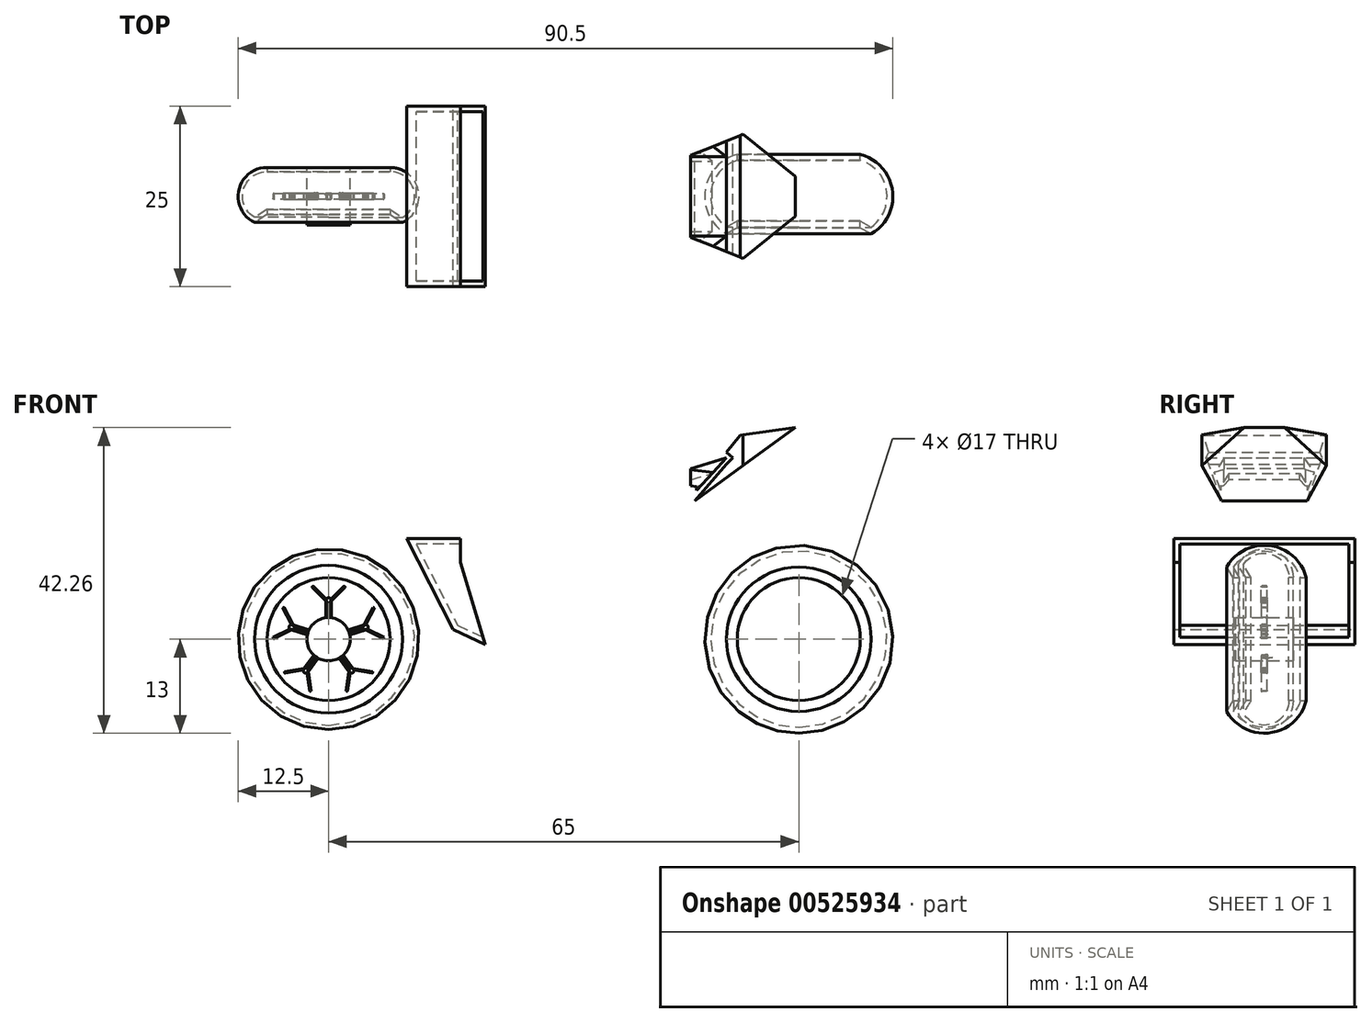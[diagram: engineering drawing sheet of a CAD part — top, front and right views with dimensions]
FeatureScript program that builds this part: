
annotation { "Feature Type Name" : "Feature", "Feature Type Description" : "" }
export const myFeature = defineFeature(function(context is Context, id is Id, definition is map)
    precondition{}
    {
        {
            var Q0;
            Q0=qCreatedBy(makeId("Front.planeOp"),FACE);
            var sketch = newSketch(context, id + "F0", { "sketchPlane" : qUnion([Q0])});
            skLineSegment(sketch, "E0", {"start": v(-48.54, 40.92) * mm, "end": v(-35.82, 48.8) * mm});
            skLineSegment(sketch, "E1", {"start": v(-21.42, 44.3) * mm, "end": v(-22.33, 41.37) * mm});
            skLineSegment(sketch, "E2", {"start": v(-12, 31.76) * mm, "end": v(-48.54, 40.92) * mm});
            skLineSegment(sketch, "E3", {"start": v(-35.82, 48.8) * mm, "end": v(-31.87, 48.8) * mm});
            skLineSegment(sketch, "E4", {"start": v(-31.87, 48.8) * mm, "end": v(-21.42, 44.3) * mm});
            skLineSegment(sketch, "E5", {"start": v(-22.33, 39.52) * mm, "end": v(-12, 31.76) * mm});
            skLineSegment(sketch, "E6", {"start": v(-22.33, 41.37) * mm, "end": v(-22.8, 39.87) * mm});
            skLineSegment(sketch, "E7", {"start": v(-22.33, 39.52) * mm, "end": v(-22.8, 39.87) * mm});
            skPoint(sketch, "E8.orphan", {"position": v(-22.9, 39.52) * mm});
            skPoint(sketch, "E9.orphan", {"position": v(-22.9, 39.95) * mm});
            skSolve(sketch);
        }
        {
            var Q0;
            Q0 = qSketchRegion(id + "F0", true);
            var Q1;
            Q1=makeQuery(id+"F0.imprint","IMPRINT",FACE,{"disambiguationData":[TD([[makeQuery(id+"F0.imprint","IMPRINT",EDGE,{"derivedFrom":sQuery(id+"F0.wireOp",EDGE,"E0")}),-1.0]])]});
            extrude(context, id + "F1", {"entities" : qUnion([Q0, Q1]), "endBound" : BoundingType.SYMMETRIC, "depth" : 16 * mm, "offsetDistance" : 25 * mm});
        }
        {
            var Q0;
            Q0=qCreatedBy(makeId("Front.planeOp"),FACE);
            var sketch = newSketch(context, id + "F2", { "sketchPlane" : qUnion([Q0])});
            skLineSegment(sketch, "E10", {"start": v(-46.44, 40.35) * mm, "end": v(-50.24, 36.38) * mm});
            skLineSegment(sketch, "E11", {"start": v(-50.24, 36.38) * mm, "end": v(-45.14, 33.46) * mm});
            skLineSegment(sketch, "E12", {"start": v(-45.14, 33.46) * mm, "end": v(-37.05, 33.46) * mm});
            skLineSegment(sketch, "E13", {"start": v(-37.05, 33.46) * mm, "end": v(-32.75, 37.72) * mm});
            skLineSegment(sketch, "E14", {"start": v(-32.75, 37.72) * mm, "end": v(-41.1, 39.88) * mm});
            skPoint(sketch, "E14.endSnap0", {"position": v(-41.1, 33.46) * mm});
            skLineSegment(sketch, "E15", {"start": v(-46.44, 40.35) * mm, "end": v(-41.51, 41.54) * mm});
            skLineSegment(sketch, "E16", {"start": v(-41.51, 41.54) * mm, "end": v(-37.94, 45.76) * mm});
            skArc(sketch, "E17", {"start": v(-23.53, 44.5) * mm, "mid": v(-30.85, 43.12) * mm, "end": v(-36.92, 38.8) * mm});
            skFitSpline(sketch, "E18", {"points": [v(-37.94, 45.76) * mm, v(-36.16, 46.98) * mm, v(-33.88, 47.49) * mm, v(-31.31, 47.24) * mm, v(-23.53, 44.5) * mm], "startDerivative": vector(8.49, 6.98) * mm, "endDerivative": vector(23.02, -8.95) * mm});
            skSolve(sketch);
        }
        {
            var Q0;
            Q0=makeQuery(id+"F2.imprint","IMPRINT",FACE,{"disambiguationData":[TD([[makeQuery(id+"F2.imprint","IMPRINT",EDGE,{"derivedFrom":sQuery(id+"F2.wireOp",EDGE,"E10")}),1.0]])]});
            extrude(context, id + "F3", {"entities" : qUnion([Q0]), "operationType" : NewBodyOperationType.ADD, "endBound" : BoundingType.SYMMETRIC, "depth" : 25 * mm, "offsetDistance" : 25 * mm});
        }
        {
            var Q0;
            Q0=makeQuery(id+"F1.opExtrude","SWEPT_EDGE",EDGE,{"disambiguationData":[OSD([sQuery(id+"F0.wireOp",EDGE,"E1"),sQuery(id+"F0.wireOp",EDGE,"E4")])]});
            fillet(context, id + "F4", {"entities" : qUnion([Q0]), "radius" : 2 * mm, "tangentPropagation" : true, "allowEdgeOverflow" : false});
        }
        {
            var Q0;
            Q0=makeQuery(id+"F1.opExtrude","SWEPT_EDGE",EDGE,{"disambiguationData":[OSD([sQuery(id+"F0.wireOp",EDGE,"E6"),sQuery(id+"F0.wireOp",EDGE,"E7")])]});
            fillet(context, id + "F5", {"entities" : qUnion([Q0]), "radius" : 2 * mm, "tangentPropagation" : true, "allowEdgeOverflow" : false});
        }
        {
            var Q0;
            Q0=makeQuery(id+"F3.opExtrude","CAP_EDGE",EDGE,{"disambiguationData":[OSD([sQuery(id+"F2.wireOp",EDGE,"E13")])],"isStart":false});
            var Q1;
            Q1=makeQuery(id+"F3.opExtrude","CAP_EDGE",EDGE,{"disambiguationData":[OSD([sQuery(id+"F2.wireOp",EDGE,"E12")])],"isStart":false});
            var Q2;
            Q2=makeQuery(id+"F3.opExtrude","CAP_EDGE",EDGE,{"disambiguationData":[OSD([sQuery(id+"F2.wireOp",EDGE,"E10")])],"isStart":false});
            var Q3;
            Q3=makeQuery(id+"F3.opExtrude","CAP_EDGE",EDGE,{"disambiguationData":[OSD([sQuery(id+"F2.wireOp",EDGE,"E11")])],"isStart":false});
            var Q4;
            Q4=makeQuery(id+"F3.opExtrude","CAP_EDGE",EDGE,{"disambiguationData":[OSD([sQuery(id+"F2.wireOp",EDGE,"E13")])],"isStart":true});
            var Q5;
            Q5=makeQuery(id+"F3.opExtrude","CAP_EDGE",EDGE,{"disambiguationData":[OSD([sQuery(id+"F2.wireOp",EDGE,"E12")])],"isStart":true});
            var Q6;
            Q6=makeQuery(id+"F3.opExtrude","CAP_EDGE",EDGE,{"disambiguationData":[OSD([sQuery(id+"F2.wireOp",EDGE,"E11")])],"isStart":true});
            var Q7;
            Q7=makeQuery(id+"F3.opExtrude","CAP_EDGE",EDGE,{"disambiguationData":[OSD([sQuery(id+"F2.wireOp",EDGE,"E10")])],"isStart":true});
            chamfer(context, id + "F6", {"entities" : qUnion([Q0, Q1, Q2, Q3, Q4, Q5, Q6, Q7]), "width" : 3 * mm, "tangentPropagation" : true});
        }
        {
            var Q0;
            Q0=qCreatedBy(makeId("Top.planeOp"),FACE);
            var sketch = newSketch(context, id + "F7", { "sketchPlane" : qUnion([Q0])});
            skLineSegment(sketch, "E19", {"start": v(-5.3, 0) * mm, "end": v(-39.6, 0) * mm, "construction": true});
            skLineSegment(sketch, "E20", {"start": v(-22.58, -8.45) * mm, "end": v(-34.27, -13.55) * mm});
            skLineSegment(sketch, "E21", {"start": v(-34.27, -13.55) * mm, "end": v(-10.35, -13.69) * mm});
            skLineSegment(sketch, "E22", {"start": v(-10.35, -13.69) * mm, "end": v(-10.35, 0) * mm});
            skLineSegment(sketch, "E23", {"start": v(-22.63, -8.45) * mm, "end": v(-11.43, -8.45) * mm});
            skLineSegment(sketch, "E24", {"start": v(-11.43, -8.45) * mm, "end": v(-11.43, 0) * mm});
            skLineSegment(sketch, "E25.MirrorCS", {"start": v(-22.58, 8.45) * mm, "end": v(-34.27, 13.55) * mm});
            skLineSegment(sketch, "E26.MirrorCS", {"start": v(-10.35, 13.69) * mm, "end": v(-10.35, 0) * mm});
            skLineSegment(sketch, "E27.MirrorCS", {"start": v(-11.43, 8.45) * mm, "end": v(-11.43, 0) * mm});
            skLineSegment(sketch, "E28.MirrorCS", {"start": v(-34.27, 13.55) * mm, "end": v(-10.35, 13.69) * mm});
            skLineSegment(sketch, "E29.MirrorCS", {"start": v(-22.63, 8.45) * mm, "end": v(-11.43, 8.45) * mm});
            skSolve(sketch);
        }
        {
            var Q0;
            {var subQ1=sQuery(id+"F7.wireOp",EDGE,"E20");Q0=makeQuery(id+"F7.imprint","IMPRINT",FACE,{"disambiguationData":[TD([[makeQuery(id+"F7.imprint","IMPRINT",EDGE,{"derivedFrom":subQ1}),1.0]])]});}
            extrude(context, id + "F8", {"entities" : qUnion([Q0]), "operationType" : NewBodyOperationType.REMOVE, "depth" : 84.6 * mm, "offsetDistance" : 25 * mm});
        }
        {
            var Q0;
            Q0=qCreatedBy(makeId("Right.planeOp"),FACE);
            var sketch = newSketch(context, id + "F9", { "sketchPlane" : qUnion([Q0])});
            skLineSegment(sketch, "E30", {"start": v(0, 53.01) * mm, "end": v(0, 33.43) * mm, "construction": true});
            skLineSegment(sketch, "E31", {"start": v(8.53, 47.82) * mm, "end": v(6.88, 48.78) * mm});
            skLineSegment(sketch, "E32", {"start": v(6.88, 48.78) * mm, "end": v(5.22, 47.78) * mm});
            skLineSegment(sketch, "E33", {"start": v(5.22, 47.78) * mm, "end": v(2.74, 47.78) * mm});
            skLineSegment(sketch, "E34", {"start": v(2.74, 47.78) * mm, "end": v(2.42, 48.02) * mm});
            skLineSegment(sketch, "E35", {"start": v(2.42, 48.02) * mm, "end": v(0, 48.02) * mm});
            skPoint(sketch, "E36.orphan", {"position": v(5.22, 49.73) * mm});
            skLineSegment(sketch, "E37", {"start": v(8.53, 47.82) * mm, "end": v(8.53, 50.14) * mm});
            skLineSegment(sketch, "E38", {"start": v(8.53, 50.14) * mm, "end": v(0, 50.14) * mm});
            skLineSegment(sketch, "E39.MirrorCS", {"start": v(-8.53, 50.14) * mm, "end": v(0, 50.14) * mm});
            skLineSegment(sketch, "E40.MirrorCS", {"start": v(-2.42, 48.02) * mm, "end": v(0, 48.02) * mm});
            skLineSegment(sketch, "E41.MirrorCS", {"start": v(-2.74, 47.78) * mm, "end": v(-2.42, 48.02) * mm});
            skLineSegment(sketch, "E42.MirrorCS", {"start": v(-5.22, 47.78) * mm, "end": v(-2.74, 47.78) * mm});
            skLineSegment(sketch, "E43.MirrorCS", {"start": v(-6.88, 48.78) * mm, "end": v(-5.22, 47.78) * mm});
            skLineSegment(sketch, "E44.MirrorCS", {"start": v(-8.53, 47.82) * mm, "end": v(-6.88, 48.78) * mm});
            skLineSegment(sketch, "E45.MirrorCS", {"start": v(-8.53, 47.82) * mm, "end": v(-8.53, 50.14) * mm});
            skSolve(sketch);
        }
        {
            var Q0;
            Q0=makeQuery(id+"F9.imprint","IMPRINT",FACE,{"disambiguationData":[TD([[makeQuery(id+"F9.imprint","IMPRINT",EDGE,{"derivedFrom":sQuery(id+"F9.wireOp",EDGE,"E31")}),-1.0]])]});
            extrude(context, id + "F10", {"entities" : qUnion([Q0]), "operationType" : NewBodyOperationType.REMOVE, "oppositeDirection" : true, "depth" : 53.16 * mm, "offsetDistance" : 25 * mm});
        }
        {
            var Q0;
            Q0=qCreatedBy(makeId("Top.planeOp"),FACE);
            var sketch = newSketch(context, id + "F11", { "sketchPlane" : qUnion([Q0])});
            skCircle(sketch, "E46", {"center": v(-48.33, 0) * mm, "radius": 7.42 * mm});
            skSolve(sketch);
        }
        {
            var Q0;
            Q0=makeQuery(id+"F11.imprint","IMPRINT",FACE,{"disambiguationData":[TD([[makeQuery(id+"F11.imprint","IMPRINT",EDGE,{"derivedFrom":sQuery(id+"F11.wireOp",EDGE,"E46")}),1.0]])]});
            extrude(context, id + "F12", {"entities" : qUnion([Q0]), "operationType" : NewBodyOperationType.REMOVE, "depth" : 52.84 * mm, "offsetDistance" : 25 * mm});
        }
        {
            var Q0;
            Q0=makeQuery(id+"F1.opExtrude","CAP_EDGE",EDGE,{"disambiguationData":[OSD([sQuery(id+"F0.wireOp",EDGE,"E0")])],"isStart":false});
            var Q1;
            Q1=makeQuery(id+"F10.boolean.opBoolean","INTERSECT",EDGE,{"derivedFrom":[makeQuery(id+"F1.opExtrude","CAP_FACE",FACE,{"disambiguationData":[OSD([sQuery(id+"F0.wireOp",EDGE,"E0"),sQuery(id+"F0.wireOp",EDGE,"E1"),sQuery(id+"F0.wireOp",EDGE,"E2"),sQuery(id+"F0.wireOp",EDGE,"E3"),sQuery(id+"F0.wireOp",EDGE,"E4"),sQuery(id+"F0.wireOp",EDGE,"E5"),sQuery(id+"F0.wireOp",EDGE,"E6"),sQuery(id+"F0.wireOp",EDGE,"E7")])],"isStart":false}),makeQuery(id+"F10.opExtrude","SWEPT_FACE",FACE,{"disambiguationData":[OSD([sQuery(id+"F9.wireOp",EDGE,"E44.MirrorCS")])]})]});
            var Q2;
            Q2=makeQuery(id+"F1.opExtrude","CAP_EDGE",EDGE,{"disambiguationData":[OSD([sQuery(id+"F0.wireOp",EDGE,"E4")])],"isStart":false});
            var Q3;
            Q3=makeQuery(id+"F1.opExtrude","CAP_EDGE",EDGE,{"disambiguationData":[OSD([sQuery(id+"F0.wireOp",EDGE,"E0")])],"isStart":true});
            var Q4;
            Q4=makeQuery(id+"F10.boolean.opBoolean","INTERSECT",EDGE,{"derivedFrom":[makeQuery(id+"F1.opExtrude","CAP_FACE",FACE,{"disambiguationData":[OSD([sQuery(id+"F0.wireOp",EDGE,"E0"),sQuery(id+"F0.wireOp",EDGE,"E1"),sQuery(id+"F0.wireOp",EDGE,"E2"),sQuery(id+"F0.wireOp",EDGE,"E3"),sQuery(id+"F0.wireOp",EDGE,"E4"),sQuery(id+"F0.wireOp",EDGE,"E5"),sQuery(id+"F0.wireOp",EDGE,"E6"),sQuery(id+"F0.wireOp",EDGE,"E7")])],"isStart":true}),makeQuery(id+"F10.opExtrude","SWEPT_FACE",FACE,{"disambiguationData":[OSD([sQuery(id+"F9.wireOp",EDGE,"E31")])]})]});
            var Q5;
            Q5=makeQuery(id+"F1.opExtrude","CAP_EDGE",EDGE,{"disambiguationData":[OSD([sQuery(id+"F0.wireOp",EDGE,"E4")])],"isStart":true});
            var Q6;
            Q6=makeQuery(id+"F10.boolean.opBoolean","COPY",EDGE,{"derivedFrom":makeQuery(id+"F10.opExtrude","SWEPT_EDGE",EDGE,{"disambiguationData":[OSD([sQuery(id+"F9.wireOp",EDGE,"E32"),sQuery(id+"F9.wireOp",EDGE,"E33")])]})});
            var Q7;
            Q7=makeQuery(id+"F10.boolean.opBoolean","COPY",EDGE,{"derivedFrom":makeQuery(id+"F10.opExtrude","SWEPT_EDGE",EDGE,{"disambiguationData":[OSD([sQuery(id+"F9.wireOp",EDGE,"E42.MirrorCS"),sQuery(id+"F9.wireOp",EDGE,"E43.MirrorCS")])]})});
            chamfer(context, id + "F13", {"entities" : qUnion([Q0, Q1, Q2, Q3, Q4, Q5, Q6, Q7]), "width" : 1 * mm, "tangentPropagation" : true});
        }
        {
            var Q0;
            {var subQ0=sQuery(id+"F2.wireOp",EDGE,"E10");Q0=makeQuery(id+"F6.opChamfer","BLEND_EDGE",EDGE,{"blendedFrom":[makeQuery(id+"F3.opExtrude","CAP_EDGE",EDGE,{"disambiguationData":[OSD([subQ0])],"isStart":false}),makeQuery(id+"F3.opExtrude","SWEPT_FACE",FACE,{"disambiguationData":[OSD([subQ0])]})],"blendedInto":[makeQuery(id+"F3.opExtrude","SWEPT_FACE",FACE,{"disambiguationData":[OSD([subQ0])]})]});}
            var Q1;
            {var subQ0=sQuery(id+"F2.wireOp",EDGE,"E11");Q1=makeQuery(id+"F6.opChamfer","BLEND_EDGE",EDGE,{"blendedFrom":[makeQuery(id+"F3.opExtrude","CAP_EDGE",EDGE,{"disambiguationData":[OSD([subQ0])],"isStart":false}),makeQuery(id+"F3.opExtrude","SWEPT_FACE",FACE,{"disambiguationData":[OSD([subQ0])]})],"blendedInto":[makeQuery(id+"F3.opExtrude","SWEPT_FACE",FACE,{"disambiguationData":[OSD([subQ0])]})]});}
            var Q2;
            {var subQ0=sQuery(id+"F2.wireOp",EDGE,"E12");Q2=makeQuery(id+"F6.opChamfer","BLEND_EDGE",EDGE,{"blendedFrom":[makeQuery(id+"F3.opExtrude","CAP_EDGE",EDGE,{"disambiguationData":[OSD([subQ0])],"isStart":false}),makeQuery(id+"F3.opExtrude","SWEPT_FACE",FACE,{"disambiguationData":[OSD([subQ0])]})],"blendedInto":[makeQuery(id+"F3.opExtrude","SWEPT_FACE",FACE,{"disambiguationData":[OSD([subQ0])]})]});}
            var Q3;
            {var subQ0=sQuery(id+"F2.wireOp",EDGE,"E13");Q3=makeQuery(id+"F6.opChamfer","BLEND_EDGE",EDGE,{"blendedFrom":[makeQuery(id+"F3.opExtrude","CAP_EDGE",EDGE,{"disambiguationData":[OSD([subQ0])],"isStart":false}),makeQuery(id+"F3.opExtrude","SWEPT_FACE",FACE,{"disambiguationData":[OSD([subQ0])]})],"blendedInto":[makeQuery(id+"F3.opExtrude","SWEPT_FACE",FACE,{"disambiguationData":[OSD([subQ0])]})]});}
            var Q4;
            Q4=makeQuery(id+"F6.opChamfer","BLEND_EDGE",EDGE,{"blendedFrom":[makeQuery(id+"F3.opExtrude","CAP_EDGE",EDGE,{"disambiguationData":[OSD([sQuery(id+"F2.wireOp",EDGE,"E10")])],"isStart":false}),makeQuery(id+"F3.opExtrude","SWEPT_FACE",FACE,{"disambiguationData":[OSD([sQuery(id+"F2.wireOp",EDGE,"E15")])]})],"blendedInto":[makeQuery(id+"F3.opExtrude","SWEPT_FACE",FACE,{"disambiguationData":[OSD([sQuery(id+"F2.wireOp",EDGE,"E15")])]})]});
            var Q5;
            {var subQ0=sQuery(id+"F2.wireOp",EDGE,"E10");Q5=makeQuery(id+"F6.opChamfer","BLEND_EDGE",EDGE,{"blendedFrom":[makeQuery(id+"F3.opExtrude","CAP_EDGE",EDGE,{"disambiguationData":[OSD([subQ0])],"isStart":true}),makeQuery(id+"F3.opExtrude","SWEPT_FACE",FACE,{"disambiguationData":[OSD([subQ0])]})],"blendedInto":[makeQuery(id+"F3.opExtrude","SWEPT_FACE",FACE,{"disambiguationData":[OSD([subQ0])]})]});}
            var Q6;
            {var subQ0=sQuery(id+"F2.wireOp",EDGE,"E11");Q6=makeQuery(id+"F6.opChamfer","BLEND_EDGE",EDGE,{"blendedFrom":[makeQuery(id+"F3.opExtrude","CAP_EDGE",EDGE,{"disambiguationData":[OSD([subQ0])],"isStart":true}),makeQuery(id+"F3.opExtrude","SWEPT_FACE",FACE,{"disambiguationData":[OSD([subQ0])]})],"blendedInto":[makeQuery(id+"F3.opExtrude","SWEPT_FACE",FACE,{"disambiguationData":[OSD([subQ0])]})]});}
            var Q7;
            {var subQ0=sQuery(id+"F2.wireOp",EDGE,"E12");Q7=makeQuery(id+"F6.opChamfer","BLEND_EDGE",EDGE,{"blendedFrom":[makeQuery(id+"F3.opExtrude","CAP_EDGE",EDGE,{"disambiguationData":[OSD([subQ0])],"isStart":true}),makeQuery(id+"F3.opExtrude","SWEPT_FACE",FACE,{"disambiguationData":[OSD([subQ0])]})],"blendedInto":[makeQuery(id+"F3.opExtrude","SWEPT_FACE",FACE,{"disambiguationData":[OSD([subQ0])]})]});}
            var Q8;
            {var subQ0=sQuery(id+"F2.wireOp",EDGE,"E13");Q8=makeQuery(id+"F6.opChamfer","BLEND_EDGE",EDGE,{"blendedFrom":[makeQuery(id+"F3.opExtrude","CAP_EDGE",EDGE,{"disambiguationData":[OSD([subQ0])],"isStart":true}),makeQuery(id+"F3.opExtrude","SWEPT_FACE",FACE,{"disambiguationData":[OSD([subQ0])]})],"blendedInto":[makeQuery(id+"F3.opExtrude","SWEPT_FACE",FACE,{"disambiguationData":[OSD([subQ0])]})]});}
            var Q9;
            Q9=makeQuery(id+"F6.opChamfer","BLEND_EDGE",EDGE,{"blendedFrom":[makeQuery(id+"F3.opExtrude","CAP_EDGE",EDGE,{"disambiguationData":[OSD([sQuery(id+"F2.wireOp",EDGE,"E10")])],"isStart":true}),makeQuery(id+"F3.opExtrude","SWEPT_FACE",FACE,{"disambiguationData":[OSD([sQuery(id+"F2.wireOp",EDGE,"E15")])]})],"blendedInto":[makeQuery(id+"F3.opExtrude","SWEPT_FACE",FACE,{"disambiguationData":[OSD([sQuery(id+"F2.wireOp",EDGE,"E15")])]})]});
            fillet(context, id + "F14", {"entities" : qUnion([Q0, Q1, Q2, Q3, Q4, Q5, Q6, Q7, Q8, Q9]), "radius" : 2 * mm, "tangentPropagation" : true, "allowEdgeOverflow" : false});
        }
        {
            var Q0;
            {var subQ1=sQuery(id+"F2.wireOp",EDGE,"E18");Q0=makeQuery(id+"F8.boolean.opBoolean","INTERSECT",EDGE,{"derivedFrom":[makeQuery(id+"F3.boolean.opBoolean","SPLIT",FACE,{"disambiguationData":[TD([makeQuery(id+"F1.opExtrude","CAP_FACE",FACE,{"disambiguationData":[OSD([sQuery(id+"F0.wireOp",EDGE,"E0"),sQuery(id+"F0.wireOp",EDGE,"E1"),sQuery(id+"F0.wireOp",EDGE,"E2"),sQuery(id+"F0.wireOp",EDGE,"E3"),sQuery(id+"F0.wireOp",EDGE,"E4"),sQuery(id+"F0.wireOp",EDGE,"E5"),sQuery(id+"F0.wireOp",EDGE,"E6"),sQuery(id+"F0.wireOp",EDGE,"E7")])],"isStart":false})])],"derivedFrom":makeQuery(id+"F3.opExtrude","SWEPT_FACE",FACE,{"disambiguationData":[OSD([subQ1])]})}),makeQuery(id+"F8.opExtrude","SWEPT_FACE",FACE,{"disambiguationData":[OSD([sQuery(id+"F7.wireOp",EDGE,"E20")])]})]});}
            var Q1;
            {var subQ1=sQuery(id+"F2.wireOp",EDGE,"E18");Q1=makeQuery(id+"F8.boolean.opBoolean","INTERSECT",EDGE,{"derivedFrom":[makeQuery(id+"F3.boolean.opBoolean","SPLIT",FACE,{"disambiguationData":[TD([makeQuery(id+"F1.opExtrude","CAP_FACE",FACE,{"disambiguationData":[OSD([sQuery(id+"F0.wireOp",EDGE,"E0"),sQuery(id+"F0.wireOp",EDGE,"E1"),sQuery(id+"F0.wireOp",EDGE,"E2"),sQuery(id+"F0.wireOp",EDGE,"E3"),sQuery(id+"F0.wireOp",EDGE,"E4"),sQuery(id+"F0.wireOp",EDGE,"E5"),sQuery(id+"F0.wireOp",EDGE,"E6"),sQuery(id+"F0.wireOp",EDGE,"E7")])],"isStart":true})])],"derivedFrom":makeQuery(id+"F3.opExtrude","SWEPT_FACE",FACE,{"disambiguationData":[OSD([subQ1])]})}),makeQuery(id+"F8.opExtrude","SWEPT_FACE",FACE,{"disambiguationData":[OSD([sQuery(id+"F7.wireOp",EDGE,"E25.MirrorCS")])]})]});}
            chamfer(context, id + "F15", {"entities" : qUnion([Q0, Q1]), "width" : 1.2 * mm, "tangentPropagation" : true});
        }
        {
            var Q0;
            Q0=qCreatedBy(makeId("Front.planeOp"),FACE);
            var sketch = newSketch(context, id + "F16", { "sketchPlane" : qUnion([Q0])});
            skLineSegment(sketch, "E47", {"start": v(-18.78, 37.42) * mm, "end": v(-13.06, 33.11) * mm});
            skLineSegment(sketch, "E48", {"start": v(-13.06, 33.11) * mm, "end": v(-4.89, 37.76) * mm});
            skLineSegment(sketch, "E49", {"start": v(-4.89, 37.76) * mm, "end": v(0, 43.09) * mm});
            skLineSegment(sketch, "E50", {"start": v(0, 43.09) * mm, "end": v(-13.7, 38.96) * mm});
            skLineSegment(sketch, "E51", {"start": v(-13.7, 38.96) * mm, "end": v(-16.73, 40.1) * mm});
            skLineSegment(sketch, "E52", {"start": v(-16.73, 40.1) * mm, "end": v(-18.78, 37.42) * mm});
            skSolve(sketch);
        }
        {
            var Q0;
            Q0 = qSketchRegion(id + "F16", true);
            var Q1;
            Q1=makeQuery(id+"F16.imprint","IMPRINT",FACE,{"disambiguationData":[TD([[makeQuery(id+"F16.imprint","IMPRINT",EDGE,{"derivedFrom":sQuery(id+"F16.wireOp",EDGE,"E47")}),1.0]])]});
            extrude(context, id + "F17", {"entities" : qUnion([Q0, Q1]), "endBound" : BoundingType.SYMMETRIC, "depth" : 15 * mm, "offsetDistance" : 25 * mm});
        }
        {
            var Q0;
            Q0=makeQuery(id+"F17.opExtrude","SWEPT_EDGE",EDGE,{"disambiguationData":[OSD([sQuery(id+"F16.wireOp",EDGE,"E51"),sQuery(id+"F16.wireOp",EDGE,"E52")])]});
            var Q1;
            Q1=makeQuery(id+"F17.opExtrude","SWEPT_EDGE",EDGE,{"disambiguationData":[OSD([sQuery(id+"F16.wireOp",EDGE,"E50"),sQuery(id+"F16.wireOp",EDGE,"E51")])]});
            fillet(context, id + "F18", {"entities" : qUnion([Q0, Q1]), "radius" : 2 * mm, "tangentPropagation" : true, "allowEdgeOverflow" : false});
        }
        {
            var Q0;
            Q0=makeQuery(id+"F17.opExtrude","CAP_EDGE",EDGE,{"disambiguationData":[OSD([sQuery(id+"F16.wireOp",EDGE,"E52")])],"isStart":false});
            var Q1;
            {var subQ0=sQuery(id+"F16.wireOp",EDGE,"E52");var subQ1=sQuery(id+"F16.wireOp",EDGE,"E51");Q1=makeQuery(id+"F18.opFillet","BLEND_EDGE",EDGE,{"blendedFrom":[makeQuery(id+"F17.opExtrude","SWEPT_EDGE",EDGE,{"disambiguationData":[OSD([subQ1,subQ0])]}),makeQuery(id+"F17.opExtrude","CAP_FACE",FACE,{"disambiguationData":[OSD([sQuery(id+"F16.wireOp",EDGE,"E47"),sQuery(id+"F16.wireOp",EDGE,"E48"),sQuery(id+"F16.wireOp",EDGE,"E49"),sQuery(id+"F16.wireOp",EDGE,"E50"),subQ1,subQ0])],"isStart":false})],"blendedInto":[makeQuery(id+"F17.opExtrude","CAP_FACE",FACE,{"disambiguationData":[OSD([sQuery(id+"F16.wireOp",EDGE,"E47"),sQuery(id+"F16.wireOp",EDGE,"E48"),sQuery(id+"F16.wireOp",EDGE,"E49"),sQuery(id+"F16.wireOp",EDGE,"E50"),subQ1,subQ0])],"isStart":false})]});}
            var Q2;
            Q2=makeQuery(id+"F17.opExtrude","CAP_EDGE",EDGE,{"disambiguationData":[OSD([sQuery(id+"F16.wireOp",EDGE,"E51")])],"isStart":false});
            var Q3;
            {var subQ0=sQuery(id+"F16.wireOp",EDGE,"E51");var subQ1=sQuery(id+"F16.wireOp",EDGE,"E50");Q3=makeQuery(id+"F18.opFillet","BLEND_EDGE",EDGE,{"blendedFrom":[makeQuery(id+"F17.opExtrude","SWEPT_EDGE",EDGE,{"disambiguationData":[OSD([subQ1,subQ0])]}),makeQuery(id+"F17.opExtrude","CAP_FACE",FACE,{"disambiguationData":[OSD([sQuery(id+"F16.wireOp",EDGE,"E47"),sQuery(id+"F16.wireOp",EDGE,"E48"),sQuery(id+"F16.wireOp",EDGE,"E49"),subQ1,subQ0,sQuery(id+"F16.wireOp",EDGE,"E52")])],"isStart":false})],"blendedInto":[makeQuery(id+"F17.opExtrude","CAP_FACE",FACE,{"disambiguationData":[OSD([sQuery(id+"F16.wireOp",EDGE,"E47"),sQuery(id+"F16.wireOp",EDGE,"E48"),sQuery(id+"F16.wireOp",EDGE,"E49"),subQ1,subQ0,sQuery(id+"F16.wireOp",EDGE,"E52")])],"isStart":false})]});}
            var Q4;
            Q4=makeQuery(id+"F17.opExtrude","CAP_EDGE",EDGE,{"disambiguationData":[OSD([sQuery(id+"F16.wireOp",EDGE,"E50")])],"isStart":false});
            var Q5;
            Q5=makeQuery(id+"F17.opExtrude","CAP_EDGE",EDGE,{"disambiguationData":[OSD([sQuery(id+"F16.wireOp",EDGE,"E50")])],"isStart":true});
            var Q6;
            {var subQ0=sQuery(id+"F16.wireOp",EDGE,"E51");var subQ1=sQuery(id+"F16.wireOp",EDGE,"E50");Q6=makeQuery(id+"F18.opFillet","BLEND_EDGE",EDGE,{"blendedFrom":[makeQuery(id+"F17.opExtrude","SWEPT_EDGE",EDGE,{"disambiguationData":[OSD([subQ1,subQ0])]}),makeQuery(id+"F17.opExtrude","CAP_FACE",FACE,{"disambiguationData":[OSD([sQuery(id+"F16.wireOp",EDGE,"E47"),sQuery(id+"F16.wireOp",EDGE,"E48"),sQuery(id+"F16.wireOp",EDGE,"E49"),subQ1,subQ0,sQuery(id+"F16.wireOp",EDGE,"E52")])],"isStart":true})],"blendedInto":[makeQuery(id+"F17.opExtrude","CAP_FACE",FACE,{"disambiguationData":[OSD([sQuery(id+"F16.wireOp",EDGE,"E47"),sQuery(id+"F16.wireOp",EDGE,"E48"),sQuery(id+"F16.wireOp",EDGE,"E49"),subQ1,subQ0,sQuery(id+"F16.wireOp",EDGE,"E52")])],"isStart":true})]});}
            var Q7;
            Q7=makeQuery(id+"F17.opExtrude","CAP_EDGE",EDGE,{"disambiguationData":[OSD([sQuery(id+"F16.wireOp",EDGE,"E51")])],"isStart":true});
            var Q8;
            {var subQ0=sQuery(id+"F16.wireOp",EDGE,"E52");var subQ1=sQuery(id+"F16.wireOp",EDGE,"E51");Q8=makeQuery(id+"F18.opFillet","BLEND_EDGE",EDGE,{"blendedFrom":[makeQuery(id+"F17.opExtrude","SWEPT_EDGE",EDGE,{"disambiguationData":[OSD([subQ1,subQ0])]}),makeQuery(id+"F17.opExtrude","CAP_FACE",FACE,{"disambiguationData":[OSD([sQuery(id+"F16.wireOp",EDGE,"E47"),sQuery(id+"F16.wireOp",EDGE,"E48"),sQuery(id+"F16.wireOp",EDGE,"E49"),sQuery(id+"F16.wireOp",EDGE,"E50"),subQ1,subQ0])],"isStart":true})],"blendedInto":[makeQuery(id+"F17.opExtrude","CAP_FACE",FACE,{"disambiguationData":[OSD([sQuery(id+"F16.wireOp",EDGE,"E47"),sQuery(id+"F16.wireOp",EDGE,"E48"),sQuery(id+"F16.wireOp",EDGE,"E49"),sQuery(id+"F16.wireOp",EDGE,"E50"),subQ1,subQ0])],"isStart":true})]});}
            var Q9;
            Q9=makeQuery(id+"F17.opExtrude","CAP_EDGE",EDGE,{"disambiguationData":[OSD([sQuery(id+"F16.wireOp",EDGE,"E52")])],"isStart":true});
            chamfer(context, id + "F19", {"entities" : qUnion([Q0, Q1, Q2, Q3, Q4, Q5, Q6, Q7, Q8, Q9]), "width" : 2 * mm, "tangentPropagation" : true});
        }
        {
            var Q0;
            Q0=makeQuery(id+"F17.opExtrude","SWEPT_FACE",FACE,{"disambiguationData":[OSD([sQuery(id+"F16.wireOp",EDGE,"E48")])]});
            var Q1;
            Q1=makeQuery(id+"F17.opExtrude","SWEPT_FACE",FACE,{"disambiguationData":[OSD([sQuery(id+"F16.wireOp",EDGE,"E49")])]});
            var Q2;
            Q2=makeQuery(id+"F17.opExtrude","SWEPT_FACE",FACE,{"disambiguationData":[OSD([sQuery(id+"F16.wireOp",EDGE,"E47")])]});
            shell(context, id + "F20", {"entities" : qUnion([Q0, Q1, Q2]), "thickness" : 1.5 * mm});
        }
        {
            var Q0;
            Q0=qCreatedBy(makeId("Front.planeOp"),FACE);
            var sketch = newSketch(context, id + "F21", { "sketchPlane" : qUnion([Q0])});
            skCircle(sketch, "E53", {"center": v(-9.22, 30.41) * mm, "radius": 1.14 * mm});
            skLineSegment(sketch, "E54", {"start": v(-10.1, 29.69) * mm, "end": v(-12.75, 32.9) * mm});
            skLineSegment(sketch, "E55", {"start": v(-12.75, 32.9) * mm, "end": v(-4.96, 37.15) * mm});
            skLineSegment(sketch, "E56", {"start": v(-4.96, 37.15) * mm, "end": v(-10.08, 31.15) * mm});
            skSolve(sketch);
        }
        {
            var Q0;
            {var subQ0=sQuery(id+"F21.wireOp",EDGE,"E53");var subQ1=makeQuery(id+"F21.imprint","INTERSECT",VERTEX,{"derivedFrom":[subQ0,sQuery(id+"F21.wireOp",EDGE,"E54")]});Q0=makeQuery(id+"F21.imprint","IMPRINT",FACE,{"disambiguationData":[TD([[makeQuery(id+"F21.imprint","IMPRINT",EDGE,{"disambiguationData":[TD([[subQ1,1.0]])],"derivedFrom":subQ0}),1.0]])]});}
            var sketch = newSketch(context, id + "F22", { "sketchPlane" : qUnion([Q0])});
            skSolve(sketch);
        }
        {
            var Q0;
            Q0 = qSketchRegion(id + "F22", true);
            var Q1;
            {var subQ0=sQuery(id+"F21.wireOp",EDGE,"E53");var subQ1=makeQuery(id+"F21.imprint","INTERSECT",VERTEX,{"derivedFrom":[subQ0,sQuery(id+"F21.wireOp",EDGE,"E54")]});Q1=makeQuery(id+"F21.imprint","IMPRINT",FACE,{"disambiguationData":[TD([[makeQuery(id+"F21.imprint","IMPRINT",EDGE,{"disambiguationData":[TD([[subQ1,1.0]])],"derivedFrom":subQ0}),1.0]])]});}
            extrude(context, id + "F23", {"entities" : qUnion([Q0, Q1]), "endBound" : BoundingType.SYMMETRIC, "depth" : 22 * mm, "offsetDistance" : 25 * mm});
        }
        {
            var Q0;
            {var subQ0=sQuery(id+"F21.wireOp",EDGE,"E54");Q0=makeQuery(id+"F21.imprint","IMPRINT",FACE,{"disambiguationData":[TD([[makeQuery(id+"F21.imprint","IMPRINT",EDGE,{"derivedFrom":subQ0}),-1.0]])]});}
            extrude(context, id + "F24", {"entities" : qUnion([Q0]), "operationType" : NewBodyOperationType.ADD, "endBound" : BoundingType.SYMMETRIC, "depth" : 18 * mm, "offsetDistance" : 25 * mm});
        }
        {
            var Q0;
            Q0=qCreatedBy(makeId("Front.planeOp"),FACE);
            var sketch = newSketch(context, id + "F25", { "sketchPlane" : qUnion([Q0])});
            skLineSegment(sketch, "E57", {"start": v(-4.38, 37.14) * mm, "end": v(0, 42.2) * mm});
            skLineSegment(sketch, "E58", {"start": v(0, 42.2) * mm, "end": v(0.87, 43.1) * mm});
            skLineSegment(sketch, "E59", {"start": v(0.87, 43.1) * mm, "end": v(0, 43.84) * mm});
            skLineSegment(sketch, "E60", {"start": v(0, 43.84) * mm, "end": v(1.88, 46.22) * mm});
            skLineSegment(sketch, "E61", {"start": v(1.88, 46.22) * mm, "end": v(9.5, 47.26) * mm});
            skLineSegment(sketch, "E62", {"start": v(9.5, 47.26) * mm, "end": v(-4.38, 37.14) * mm});
            skSolve(sketch);
        }
        {
            var Q0;
            Q0=makeQuery(id+"F25.imprint","IMPRINT",FACE,{"disambiguationData":[TD([[makeQuery(id+"F25.imprint","IMPRINT",EDGE,{"derivedFrom":sQuery(id+"F25.wireOp",EDGE,"E57")}),-1.0]])]});
            extrude(context, id + "F26", {"entities" : qUnion([Q0]), "endBound" : BoundingType.SYMMETRIC, "depth" : 25 * mm, "offsetDistance" : 25 * mm});
        }
        {
            var Q0;
            Q0=qCreatedBy(makeId("Top.planeOp"),FACE);
            var sketch = newSketch(context, id + "F27", { "sketchPlane" : qUnion([Q0])});
            skLineSegment(sketch, "E63", {"start": v(12.92, 0) * mm, "end": v(-9.34, 0) * mm, "construction": true});
            skLineSegment(sketch, "E64", {"start": v(12.92, 0) * mm, "end": v(2.3, 8.61) * mm});
            skLineSegment(sketch, "E65", {"start": v(2.3, 8.61) * mm, "end": v(-4.94, 5.67) * mm});
            skLineSegment(sketch, "E66", {"start": v(-4.94, 5.67) * mm, "end": v(-4.94, 0) * mm});
            skLineSegment(sketch, "E67.MirrorCS", {"start": v(2.3, -8.61) * mm, "end": v(-4.94, -5.67) * mm});
            skLineSegment(sketch, "E68.MirrorCS", {"start": v(12.92, 0) * mm, "end": v(2.3, -8.61) * mm});
            skLineSegment(sketch, "E69.MirrorCS", {"start": v(-4.94, -5.67) * mm, "end": v(-4.94, 0) * mm});
            skSolve(sketch);
        }
        {
            var Q0;
            Q0=makeQuery(id+"F27.imprint","IMPRINT",FACE,{"disambiguationData":[TD([[makeQuery(id+"F27.imprint","IMPRINT",EDGE,{"derivedFrom":sQuery(id+"F27.wireOp",EDGE,"E64")}),1.0]])]});
            extrude(context, id + "F28", {"entities" : qUnion([Q0]), "operationType" : NewBodyOperationType.INTERSECT, "depth" : 101.85 * mm, "offsetDistance" : 25 * mm});
        }
        {
            var Q0;
            Q0=qCreatedBy(makeId("Front.planeOp"),FACE);
            var sketch = newSketch(context, id + "F29", { "sketchPlane" : qUnion([Q0])});
            skCircle(sketch, "E70", {"center": v(-55, 18) * mm, "radius": 12.5 * mm});
            skSolve(sketch);
        }
        {
            var Q0;
            Q0=makeQuery(id+"F29.imprint","IMPRINT",FACE,{"disambiguationData":[TD([[makeQuery(id+"F29.imprint","IMPRINT",EDGE,{"derivedFrom":sQuery(id+"F29.wireOp",EDGE,"E70")}),1.0]])]});
            extrude(context, id + "F30", {"entities" : qUnion([Q0]), "endBound" : BoundingType.SYMMETRIC, "depth" : 8 * mm, "offsetDistance" : 25 * mm});
        }
        {
            var Q0;
            Q0=makeQuery(id+"F30.opExtrude","CAP_EDGE",EDGE,{"disambiguationData":[OSD([sQuery(id+"F29.wireOp",EDGE,"E70")])],"isStart":false});
            var Q1;
            Q1=makeQuery(id+"F30.opExtrude","CAP_EDGE",EDGE,{"disambiguationData":[OSD([sQuery(id+"F29.wireOp",EDGE,"E70")])],"isStart":true});
            fillet(context, id + "F31", {"entities" : qUnion([Q0, Q1]), "radius" : 4 * mm, "tangentPropagation" : true, "allowEdgeOverflow" : false});
        }
        {
            var Q0;
            Q0=makeQuery(id+"F30.opExtrude","CAP_FACE",FACE,{"disambiguationData":[OSD([sQuery(id+"F29.wireOp",EDGE,"E70")])],"isStart":false});
            extrude(context, id + "F32", {"entities" : qUnion([Q0]), "operationType" : NewBodyOperationType.REMOVE, "oppositeDirection" : true, "depth" : 25 * mm, "offsetDistance" : 25 * mm});
        }
        {
            var Q0;
            {var subQ0=sQuery(id+"F29.wireOp",EDGE,"E70");Q0=makeQuery(id+"F32.boolean.opBoolean","MERGE",EDGE,{"derivedFrom":[makeQuery(id+"F31.opFillet","BLEND_EDGE",EDGE,{"blendedFrom":[makeQuery(id+"F30.opExtrude","CAP_EDGE",EDGE,{"disambiguationData":[OSD([subQ0])],"isStart":false}),makeQuery(id+"F30.opExtrude","CAP_FACE",FACE,{"disambiguationData":[OSD([subQ0])],"isStart":false})],"blendedInto":[makeQuery(id+"F30.opExtrude","CAP_FACE",FACE,{"disambiguationData":[OSD([subQ0])],"isStart":false})]}),makeQuery(id+"F32.opExtrude","CAP_EDGE",EDGE,{"disambiguationData":[OSD([subQ0])],"isStart":true})]});}
            var Q1;
            {var subQ0=sQuery(id+"F29.wireOp",EDGE,"E70");Q1=makeQuery(id+"F31.opFillet","BLEND_EDGE",EDGE,{"blendedFrom":[makeQuery(id+"F30.opExtrude","CAP_EDGE",EDGE,{"disambiguationData":[OSD([subQ0])],"isStart":true}),makeQuery(id+"F30.opExtrude","CAP_FACE",FACE,{"disambiguationData":[OSD([subQ0])],"isStart":true})],"blendedInto":[makeQuery(id+"F30.opExtrude","CAP_FACE",FACE,{"disambiguationData":[OSD([subQ0])],"isStart":true})]});}
            chamfer(context, id + "F33", {"entities" : qUnion([Q0, Q1]), "width" : 1.2 * mm, "tangentPropagation" : true});
        }
        {
            var Q0;
            Q0=makeQuery(id+"F32.boolean.opBoolean","COPY",FACE,{"derivedFrom":makeQuery(id+"F32.opExtrude","SWEPT_FACE",FACE,{"disambiguationData":[OSD([sQuery(id+"F29.wireOp",EDGE,"E70")])]})});
            shell(context, id + "F34", {"entities" : qUnion([Q0]), "thickness" : 0.6 * mm});
        }
        {
            var Q0;
            Q0=qCreatedBy(makeId("Front.planeOp"),FACE);
            var sketch = newSketch(context, id + "F35", { "sketchPlane" : qUnion([Q0])});
            skCircle(sketch, "E71", {"center": v(-55, 18) * mm, "radius": 3 * mm});
            skLineSegment(sketch, "E72", {"start": v(-55, 18) * mm, "end": v(-55, 32.96) * mm, "construction": true});
            skLineSegment(sketch, "E73", {"start": v(-54.63, 20.98) * mm, "end": v(-54.63, 23.27) * mm});
            skLineSegment(sketch, "E74", {"start": v(-54.63, 23.27) * mm, "end": v(-52.72, 25.21) * mm});
            skLineSegment(sketch, "E75", {"start": v(-54.83, 21) * mm, "end": v(-54.83, 23.01) * mm});
            skLineSegment(sketch, "E76", {"start": v(-54.66, 23.52) * mm, "end": v(-52.86, 25.35) * mm});
            skLineSegment(sketch, "E77", {"start": v(-52.86, 25.35) * mm, "end": v(-52.72, 25.21) * mm});
            skLineSegment(sketch, "E78.MirrorCS", {"start": v(-55.17, 21) * mm, "end": v(-55.17, 23.01) * mm});
            skLineSegment(sketch, "E79.MirrorCS", {"start": v(-55.37, 23.27) * mm, "end": v(-57.28, 25.21) * mm});
            skLineSegment(sketch, "E80.MirrorCS", {"start": v(-55.34, 23.52) * mm, "end": v(-57.14, 25.35) * mm});
            skLineSegment(sketch, "E81.MirrorCS", {"start": v(-57.14, 25.35) * mm, "end": v(-57.28, 25.21) * mm});
            skLineSegment(sketch, "E82.MirrorCS", {"start": v(-55.37, 20.98) * mm, "end": v(-55.37, 23.27) * mm});
            skArc(sketch, "E83", {"start": v(-55.17, 23.01) * mm, "mid": v(-55, 22.97) * mm, "end": v(-54.83, 23.01) * mm});
            skPoint(sketch, "E84.orphan", {"position": v(-54.83, 23.35) * mm});
            skPoint(sketch, "E85.orphan", {"position": v(-55.17, 23.35) * mm});
            skArc(sketch, "E86.trimOffspring", {"start": v(-54.66, 23.52) * mm, "mid": v(-55, 23.73) * mm, "end": v(-55.34, 23.52) * mm});
            skLineSegment(sketch, "E87.1.0", {"start": v(-57.72, 19.27) * mm, "end": v(-59.9, 19.98) * mm});
            skLineSegment(sketch, "E87.1.1", {"start": v(-57.8, 19.09) * mm, "end": v(-59.72, 19.7) * mm});
            skLineSegment(sketch, "E87.1.2", {"start": v(-57.9, 18.77) * mm, "end": v(-59.82, 19.39) * mm});
            skLineSegment(sketch, "E87.1.3", {"start": v(-57.95, 18.57) * mm, "end": v(-60.13, 19.28) * mm});
            skArc(sketch, "E87.1.4", {"start": v(-59.82, 19.39) * mm, "mid": v(-59.73, 19.54) * mm, "end": v(-59.72, 19.7) * mm});
            skArc(sketch, "E87.1.5", {"start": v(-60.15, 20.03) * mm, "mid": v(-60.45, 19.77) * mm, "end": v(-60.36, 19.39) * mm});
            skLineSegment(sketch, "E87.1.6", {"start": v(-60.15, 20.03) * mm, "end": v(-61.33, 22.3) * mm});
            skLineSegment(sketch, "E87.1.7", {"start": v(-60.13, 19.28) * mm, "end": v(-62.57, 18.06) * mm});
            skLineSegment(sketch, "E87.1.8", {"start": v(-59.9, 19.98) * mm, "end": v(-61.16, 22.4) * mm});
            skLineSegment(sketch, "E87.1.9", {"start": v(-60.36, 19.39) * mm, "end": v(-62.65, 18.24) * mm});
            skLineSegment(sketch, "E87.1.10", {"start": v(-62.65, 18.24) * mm, "end": v(-62.57, 18.06) * mm});
            skLineSegment(sketch, "E87.1.11", {"start": v(-61.33, 22.3) * mm, "end": v(-61.16, 22.4) * mm});
            skLineSegment(sketch, "E87.2.0", {"start": v(-57.05, 15.8) * mm, "end": v(-58.4, 13.95) * mm});
            skLineSegment(sketch, "E87.2.1", {"start": v(-56.9, 15.68) * mm, "end": v(-58.08, 14.04) * mm});
            skLineSegment(sketch, "E87.2.2", {"start": v(-56.62, 15.48) * mm, "end": v(-57.81, 13.84) * mm});
            skLineSegment(sketch, "E87.2.3", {"start": v(-56.45, 15.38) * mm, "end": v(-57.8, 13.52) * mm});
            skArc(sketch, "E87.2.4", {"start": v(-57.81, 13.84) * mm, "mid": v(-57.92, 13.98) * mm, "end": v(-58.08, 14.04) * mm});
            skArc(sketch, "E87.2.5", {"start": v(-58.52, 13.73) * mm, "mid": v(-58.37, 13.37) * mm, "end": v(-57.97, 13.34) * mm});
            skLineSegment(sketch, "E87.2.6", {"start": v(-58.52, 13.73) * mm, "end": v(-61.05, 13.3) * mm});
            skLineSegment(sketch, "E87.2.7", {"start": v(-57.8, 13.52) * mm, "end": v(-57.4, 10.82) * mm});
            skLineSegment(sketch, "E87.2.8", {"start": v(-58.4, 13.95) * mm, "end": v(-61.08, 13.5) * mm});
            skLineSegment(sketch, "E87.2.9", {"start": v(-57.97, 13.34) * mm, "end": v(-57.6, 10.8) * mm});
            skLineSegment(sketch, "E87.2.10", {"start": v(-57.6, 10.8) * mm, "end": v(-57.4, 10.82) * mm});
            skLineSegment(sketch, "E87.2.11", {"start": v(-61.05, 13.3) * mm, "end": v(-61.08, 13.5) * mm});
            skLineSegment(sketch, "E87.3.0", {"start": v(-53.55, 15.38) * mm, "end": v(-52.2, 13.52) * mm});
            skLineSegment(sketch, "E87.3.1", {"start": v(-53.38, 15.48) * mm, "end": v(-52.19, 13.84) * mm});
            skLineSegment(sketch, "E87.3.2", {"start": v(-53.1, 15.68) * mm, "end": v(-51.92, 14.04) * mm});
            skLineSegment(sketch, "E87.3.3", {"start": v(-52.95, 15.8) * mm, "end": v(-51.6, 13.95) * mm});
            skArc(sketch, "E87.3.4", {"start": v(-51.92, 14.04) * mm, "mid": v(-52.08, 13.98) * mm, "end": v(-52.19, 13.84) * mm});
            skArc(sketch, "E87.3.5", {"start": v(-52.03, 13.34) * mm, "mid": v(-51.63, 13.37) * mm, "end": v(-51.48, 13.73) * mm});
            skLineSegment(sketch, "E87.3.6", {"start": v(-52.03, 13.34) * mm, "end": v(-52.4, 10.8) * mm});
            skLineSegment(sketch, "E87.3.7", {"start": v(-51.6, 13.95) * mm, "end": v(-48.92, 13.5) * mm});
            skLineSegment(sketch, "E87.3.8", {"start": v(-52.2, 13.52) * mm, "end": v(-52.6, 10.82) * mm});
            skLineSegment(sketch, "E87.3.9", {"start": v(-51.48, 13.73) * mm, "end": v(-48.95, 13.3) * mm});
            skLineSegment(sketch, "E87.3.10", {"start": v(-48.95, 13.3) * mm, "end": v(-48.92, 13.5) * mm});
            skLineSegment(sketch, "E87.3.11", {"start": v(-52.4, 10.8) * mm, "end": v(-52.6, 10.82) * mm});
            skLineSegment(sketch, "E87.4.0", {"start": v(-52.05, 18.57) * mm, "end": v(-49.87, 19.28) * mm});
            skLineSegment(sketch, "E87.4.1", {"start": v(-52.1, 18.77) * mm, "end": v(-50.18, 19.39) * mm});
            skLineSegment(sketch, "E87.4.2", {"start": v(-52.2, 19.09) * mm, "end": v(-50.28, 19.7) * mm});
            skLineSegment(sketch, "E87.4.3", {"start": v(-52.28, 19.27) * mm, "end": v(-50.1, 19.98) * mm});
            skArc(sketch, "E87.4.4", {"start": v(-50.28, 19.7) * mm, "mid": v(-50.27, 19.54) * mm, "end": v(-50.18, 19.39) * mm});
            skArc(sketch, "E87.4.5", {"start": v(-49.64, 19.39) * mm, "mid": v(-49.55, 19.77) * mm, "end": v(-49.85, 20.03) * mm});
            skLineSegment(sketch, "E87.4.6", {"start": v(-49.64, 19.39) * mm, "end": v(-47.35, 18.24) * mm});
            skLineSegment(sketch, "E87.4.7", {"start": v(-50.1, 19.98) * mm, "end": v(-48.84, 22.4) * mm});
            skLineSegment(sketch, "E87.4.8", {"start": v(-49.87, 19.28) * mm, "end": v(-47.43, 18.06) * mm});
            skLineSegment(sketch, "E87.4.9", {"start": v(-49.85, 20.03) * mm, "end": v(-48.67, 22.3) * mm});
            skLineSegment(sketch, "E87.4.10", {"start": v(-48.67, 22.3) * mm, "end": v(-48.84, 22.4) * mm});
            skLineSegment(sketch, "E87.4.11", {"start": v(-47.35, 18.24) * mm, "end": v(-47.43, 18.06) * mm});
            skSolve(sketch);
        }
        {
            var Q0;
            Q0=qCreatedBy(makeId("Front.planeOp"),FACE);
            var sketch = newSketch(context, id + "F36", { "sketchPlane" : qUnion([Q0])});
            skCircle(sketch, "E88", {"center": v(10, 18) * mm, "radius": 13 * mm});
            skSolve(sketch);
        }
        {
            var Q0;
            Q0=makeQuery(id+"F36.imprint","IMPRINT",FACE,{"disambiguationData":[TD([[makeQuery(id+"F36.imprint","IMPRINT",EDGE,{"derivedFrom":sQuery(id+"F36.wireOp",EDGE,"E88")}),1.0]])]});
            extrude(context, id + "F37", {"entities" : qUnion([Q0]), "endBound" : BoundingType.SYMMETRIC, "depth" : 12 * mm, "offsetDistance" : 25 * mm});
        }
        {
            var Q0;
            Q0=makeQuery(id+"F37.opExtrude","CAP_EDGE",EDGE,{"disambiguationData":[OSD([sQuery(id+"F36.wireOp",EDGE,"E88")])],"isStart":false});
            var Q1;
            Q1=makeQuery(id+"F37.opExtrude","CAP_EDGE",EDGE,{"disambiguationData":[OSD([sQuery(id+"F36.wireOp",EDGE,"E88")])],"isStart":true});
            fillet(context, id + "F38", {"entities" : qUnion([Q0, Q1]), "radius" : 6 * mm, "tangentPropagation" : true, "allowEdgeOverflow" : false});
        }
        {
            var Q0;
            Q0=makeQuery(id+"F37.opExtrude","CAP_FACE",FACE,{"disambiguationData":[OSD([sQuery(id+"F36.wireOp",EDGE,"E88")])],"isStart":false});
            extrude(context, id + "F39", {"entities" : qUnion([Q0]), "operationType" : NewBodyOperationType.REMOVE, "oppositeDirection" : true, "depth" : 25 * mm, "offsetDistance" : 25 * mm});
        }
        {
            var Q0;
            {var subQ0=sQuery(id+"F36.wireOp",EDGE,"E88");Q0=makeQuery(id+"F39.boolean.opBoolean","MERGE",EDGE,{"derivedFrom":[makeQuery(id+"F38.opFillet","BLEND_EDGE",EDGE,{"blendedFrom":[makeQuery(id+"F37.opExtrude","CAP_EDGE",EDGE,{"disambiguationData":[OSD([subQ0])],"isStart":false}),makeQuery(id+"F37.opExtrude","CAP_FACE",FACE,{"disambiguationData":[OSD([subQ0])],"isStart":false})],"blendedInto":[makeQuery(id+"F37.opExtrude","CAP_FACE",FACE,{"disambiguationData":[OSD([subQ0])],"isStart":false})]}),makeQuery(id+"F39.opExtrude","CAP_EDGE",EDGE,{"disambiguationData":[OSD([subQ0])],"isStart":true})]});}
            var Q1;
            {var subQ0=sQuery(id+"F36.wireOp",EDGE,"E88");Q1=makeQuery(id+"F38.opFillet","BLEND_EDGE",EDGE,{"blendedFrom":[makeQuery(id+"F37.opExtrude","CAP_EDGE",EDGE,{"disambiguationData":[OSD([subQ0])],"isStart":true}),makeQuery(id+"F37.opExtrude","CAP_FACE",FACE,{"disambiguationData":[OSD([subQ0])],"isStart":true})],"blendedInto":[makeQuery(id+"F37.opExtrude","CAP_FACE",FACE,{"disambiguationData":[OSD([subQ0])],"isStart":true})]});}
            chamfer(context, id + "F40", {"entities" : qUnion([Q0, Q1]), "width" : 2 * mm, "tangentPropagation" : true});
        }
        {
            var Q0;
            Q0=qCreatedBy(makeId("Front.planeOp"),FACE);
            var sketch = newSketch(context, id + "F41", { "sketchPlane" : qUnion([Q0])});
            skCircle(sketch, "E89", {"center": v(10, 18) * mm, "radius": 8.5 * mm});
            skSolve(sketch);
        }
        {
            var Q0;
            Q0=makeQuery(id+"F41.imprint","IMPRINT",FACE,{"disambiguationData":[TD([[makeQuery(id+"F41.imprint","IMPRINT",EDGE,{"derivedFrom":sQuery(id+"F41.wireOp",EDGE,"E89")}),1.0]])]});
            var Q1;
            Q1 = qSketchRegion(id + "F41", true);
            extrude(context, id + "F42", {"entities" : qUnion([Q0, Q1]), "operationType" : NewBodyOperationType.REMOVE, "endBound" : BoundingType.SYMMETRIC, "depth" : 25 * mm, "offsetDistance" : 25 * mm});
        }
        {
            var Q0;
            Q0=makeQuery(id+"F42.boolean.opBoolean","COPY",FACE,{"derivedFrom":makeQuery(id+"F42.opExtrude","SWEPT_FACE",FACE,{"disambiguationData":[OSD([sQuery(id+"F41.wireOp",EDGE,"E89")])]})});
            shell(context, id + "F43", {"entities" : qUnion([Q0]), "thickness" : 0.8 * mm});
        }
        {
            var Q0;
            Q0=qCreatedBy(makeId("Front.planeOp"),FACE);
            var sketch = newSketch(context, id + "F44", { "sketchPlane" : qUnion([Q0])});
            skLineSegment(sketch, "E90", {"start": v(-36.77, 31.93) * mm, "end": v(-44.2, 31.93) * mm});
            skLineSegment(sketch, "E91", {"start": v(-44.2, 31.93) * mm, "end": v(-37.76, 19.34) * mm});
            skLineSegment(sketch, "E92", {"start": v(-37.76, 19.34) * mm, "end": v(-33.34, 17.22) * mm});
            skLineSegment(sketch, "E93", {"start": v(-33.34, 17.22) * mm, "end": v(-36.77, 28.6) * mm});
            skLineSegment(sketch, "E94", {"start": v(-36.77, 28.6) * mm, "end": v(-36.77, 31.93) * mm});
            skSolve(sketch);
        }
        {
            var Q0;
            Q0=makeQuery(id+"F44.imprint","IMPRINT",FACE,{"disambiguationData":[TD([[makeQuery(id+"F44.imprint","IMPRINT",EDGE,{"derivedFrom":sQuery(id+"F44.wireOp",EDGE,"E90")}),1.0]])]});
            extrude(context, id + "F45", {"entities" : qUnion([Q0]), "endBound" : BoundingType.SYMMETRIC, "depth" : 25 * mm, "offsetDistance" : 25 * mm});
        }
        {
            var Q0;
            Q0=makeQuery(id+"F45.opExtrude","SWEPT_FACE",FACE,{"disambiguationData":[OSD([sQuery(id+"F44.wireOp",EDGE,"E94")])]});
            var Q1;
            Q1=makeQuery(id+"F45.opExtrude","SWEPT_FACE",FACE,{"disambiguationData":[OSD([sQuery(id+"F44.wireOp",EDGE,"E93")])]});
            shell(context, id + "F46", {"entities" : qUnion([Q0, Q1]), "thickness" : 0.8 * mm});
        }
        {
            var Q0;
            {var subQ0=sQuery(id+"F35.wireOp",EDGE,"E71");var subQ8=makeQuery(id+"F35.imprint","INTERSECT",VERTEX,{"derivedFrom":[subQ0,sQuery(id+"F35.wireOp",EDGE,"E87.4.0")]});Q0=makeQuery(id+"F35.imprint","IMPRINT",FACE,{"disambiguationData":[TD([[makeQuery(id+"F35.imprint","IMPRINT",EDGE,{"disambiguationData":[TD([[subQ8,-1.0]])],"derivedFrom":subQ0}),1.0]])]});}
            extrude(context, id + "F47", {"entities" : qUnion([Q0]), "endBound" : BoundingType.SYMMETRIC, "depth" : 8 * mm, "offsetDistance" : 25 * mm});
        }
        {
            var Q0;
            {var subQ0=sQuery(id+"F35.wireOp",EDGE,"E73");Q0=makeQuery(id+"F35.imprint","IMPRINT",FACE,{"disambiguationData":[TD([[makeQuery(id+"F35.imprint","IMPRINT",EDGE,{"derivedFrom":subQ0}),1.0]])]});}
            extrude(context, id + "F48", {"entities" : qUnion([Q0]), "operationType" : NewBodyOperationType.ADD, "endBound" : BoundingType.SYMMETRIC, "oppositeDirection" : true, "depth" : 0.8 * mm, "offsetDistance" : 25 * mm});
        }
        {
            var Q0;
            Q0=makeQuery(id+"F48.opExtrude","CAP_EDGE",EDGE,{"disambiguationData":[OSD([sQuery(id+"F35.wireOp",EDGE,"E79.MirrorCS")])],"isStart":true});
            var Q1;
            Q1=makeQuery(id+"F48.opExtrude","CAP_EDGE",EDGE,{"disambiguationData":[OSD([sQuery(id+"F35.wireOp",EDGE,"E80.MirrorCS")])],"isStart":true});
            var Q2;
            Q2=makeQuery(id+"F48.opExtrude","CAP_EDGE",EDGE,{"disambiguationData":[OSD([sQuery(id+"F35.wireOp",EDGE,"E80.MirrorCS")])],"isStart":false});
            var Q3;
            Q3=makeQuery(id+"F48.opExtrude","CAP_EDGE",EDGE,{"disambiguationData":[OSD([sQuery(id+"F35.wireOp",EDGE,"E74")])],"isStart":true});
            var Q4;
            Q4=makeQuery(id+"F48.opExtrude","CAP_EDGE",EDGE,{"disambiguationData":[OSD([sQuery(id+"F35.wireOp",EDGE,"E76")])],"isStart":true});
            var Q5;
            Q5=makeQuery(id+"F48.opExtrude","CAP_EDGE",EDGE,{"disambiguationData":[OSD([sQuery(id+"F35.wireOp",EDGE,"E73")])],"isStart":true});
            var Q6;
            Q6=makeQuery(id+"F48.opExtrude","CAP_EDGE",EDGE,{"disambiguationData":[OSD([sQuery(id+"F35.wireOp",EDGE,"E73")])],"isStart":false});
            var Q7;
            Q7=makeQuery(id+"F48.opExtrude","CAP_EDGE",EDGE,{"disambiguationData":[OSD([sQuery(id+"F35.wireOp",EDGE,"E75")])],"isStart":true});
            var Q8;
            Q8=makeQuery(id+"F48.opExtrude","CAP_EDGE",EDGE,{"disambiguationData":[OSD([sQuery(id+"F35.wireOp",EDGE,"E78.MirrorCS")])],"isStart":false});
            var Q9;
            Q9=makeQuery(id+"F48.opExtrude","CAP_EDGE",EDGE,{"disambiguationData":[OSD([sQuery(id+"F35.wireOp",EDGE,"E78.MirrorCS")])],"isStart":true});
            var Q10;
            Q10=makeQuery(id+"F48.opExtrude","CAP_EDGE",EDGE,{"disambiguationData":[OSD([sQuery(id+"F35.wireOp",EDGE,"E82.MirrorCS")])],"isStart":true});
            var Q11;
            Q11=makeQuery(id+"F48.opExtrude","CAP_EDGE",EDGE,{"disambiguationData":[OSD([sQuery(id+"F35.wireOp",EDGE,"E74")])],"isStart":false});
            var Q12;
            Q12=makeQuery(id+"F48.opExtrude","CAP_EDGE",EDGE,{"disambiguationData":[OSD([sQuery(id+"F35.wireOp",EDGE,"E76")])],"isStart":false});
            var Q13;
            Q13=makeQuery(id+"F48.opExtrude","CAP_EDGE",EDGE,{"disambiguationData":[OSD([sQuery(id+"F35.wireOp",EDGE,"E79.MirrorCS")])],"isStart":false});
            var Q14;
            Q14=makeQuery(id+"F48.opExtrude","CAP_EDGE",EDGE,{"disambiguationData":[OSD([sQuery(id+"F35.wireOp",EDGE,"E82.MirrorCS")])],"isStart":false});
            var Q15;
            Q15=makeQuery(id+"F48.opExtrude","CAP_EDGE",EDGE,{"disambiguationData":[OSD([sQuery(id+"F35.wireOp",EDGE,"E86.trimOffspring")])],"isStart":true});
            var Q16;
            Q16=makeQuery(id+"F48.opExtrude","CAP_EDGE",EDGE,{"disambiguationData":[OSD([sQuery(id+"F35.wireOp",EDGE,"E83")])],"isStart":true});
            var Q17;
            Q17=makeQuery(id+"F48.opExtrude","CAP_FACE",FACE,{"disambiguationData":[OSD([sQuery(id+"F35.wireOp",EDGE,"E71"),sQuery(id+"F35.wireOp",EDGE,"E73"),sQuery(id+"F35.wireOp",EDGE,"E74"),sQuery(id+"F35.wireOp",EDGE,"E75"),sQuery(id+"F35.wireOp",EDGE,"E76"),sQuery(id+"F35.wireOp",EDGE,"E77"),sQuery(id+"F35.wireOp",EDGE,"E78.MirrorCS"),sQuery(id+"F35.wireOp",EDGE,"E79.MirrorCS"),sQuery(id+"F35.wireOp",EDGE,"E80.MirrorCS"),sQuery(id+"F35.wireOp",EDGE,"E81.MirrorCS"),sQuery(id+"F35.wireOp",EDGE,"E82.MirrorCS"),sQuery(id+"F35.wireOp",EDGE,"E83"),sQuery(id+"F35.wireOp",EDGE,"E86.trimOffspring")])],"isStart":false});
            var Q18;
            Q18=makeQuery(id+"F48.opExtrude","CAP_EDGE",EDGE,{"disambiguationData":[OSD([sQuery(id+"F35.wireOp",EDGE,"E86.trimOffspring")])],"isStart":false});
            var Q19;
            Q19=makeQuery(id+"F48.opExtrude","CAP_EDGE",EDGE,{"disambiguationData":[OSD([sQuery(id+"F35.wireOp",EDGE,"E83")])],"isStart":false});
            fillet(context, id + "F49", {"entities" : qUnion([Q0, Q1, Q2, Q3, Q4, Q5, Q6, Q7, Q8, Q9, Q10, Q11, Q12, Q13, Q14, Q15, Q16, Q17, Q18, Q19]), "radius" : 0.1 * mm, "tangentPropagation" : true, "allowEdgeOverflow" : false});
        }
        {
            var Q0;
            Q0=makeQuery(id+"F47.opExtrude","SWEPT_BODY",BODY,{"disambiguationData":[OSD([sQuery(id+"F35.wireOp",EDGE,"E71")])]});
            var Q1;
            Q1=makeQuery(id+"F47.opExtrude","CAP_EDGE",EDGE,{"disambiguationData":[OSD([sQuery(id+"F35.wireOp",EDGE,"E71")])],"isStart":false});
            circularPattern(context, id + "F50", {"entities" : qUnion([Q0]), "axis" : qUnion([Q1]), "angle" : 360 * degree, "instanceCount" : 5, "equalSpace" : true});
        }
    });
